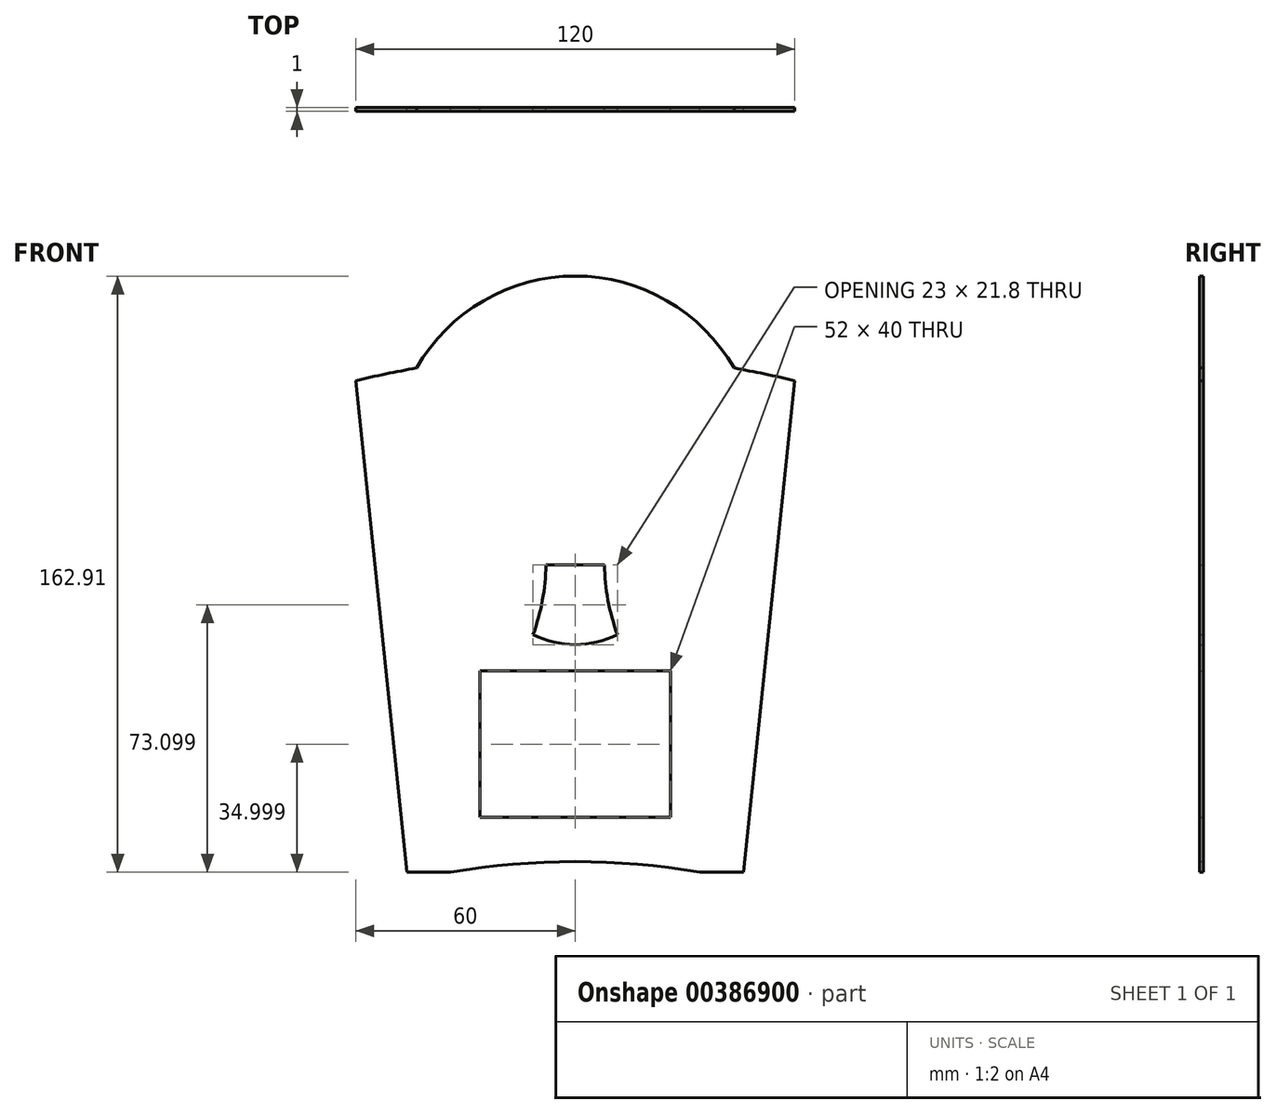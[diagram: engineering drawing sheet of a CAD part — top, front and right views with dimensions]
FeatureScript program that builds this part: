
annotation { "Feature Type Name" : "Feature", "Feature Type Description" : "" }
export const myFeature = defineFeature(function(context is Context, id is Id, definition is map)
    precondition{}
    {
        {
            var Q0;
            Q0=qCreatedBy(makeId("Front.planeOp"),FACE);
            var sketch = newSketch(context, id + "F0", { "sketchPlane" : qUnion([Q0])});
            skLineSegment(sketch, "E0", {"start": v(-46, -93.4) * mm, "end": v(-46, -111.03) * mm, "construction": true});
            skLineSegment(sketch, "E1", {"start": v(-60, 111.9) * mm, "end": v(-60, 93.46) * mm, "construction": true});
            skLineSegment(sketch, "E2", {"start": v(0, 80) * mm, "end": v(15.47, 80) * mm, "construction": true});
            skLineSegment(sketch, "E3", {"start": v(0, -80) * mm, "end": v(14.67, -80) * mm, "construction": true});
            skArc(sketch, "E4", {"start": v(0, 80) * mm, "mid": v(-25.06, 73.27) * mm, "end": v(-43.37, 54.88) * mm});
            skArc(sketch, "E5", {"start": v(0, -80) * mm, "mid": v(-17.06, -80.73) * mm, "end": v(-34, -82.91) * mm});
            skLineSegment(sketch, "E6", {"start": v(-46, -82.91) * mm, "end": v(-60, 51.36) * mm});
            skLineSegment(sketch, "E7", {"start": v(0, 0) * mm, "end": v(0, 20.52) * mm, "construction": true});
            skLineSegment(sketch, "E8", {"start": v(-46, -82.91) * mm, "end": v(-34, -82.91) * mm});
            skArc(sketch, "E9", {"start": v(-60, 51.36) * mm, "mid": v(-51.72, 53.26) * mm, "end": v(-43.37, 54.88) * mm});
            skArc(sketch, "E10.MirrorCS", {"start": v(0, 80) * mm, "mid": v(25.06, 73.27) * mm, "end": v(43.37, 54.88) * mm});
            skArc(sketch, "E11.MirrorCS", {"start": v(60, 51.36) * mm, "mid": v(51.72, 53.26) * mm, "end": v(43.37, 54.88) * mm});
            skLineSegment(sketch, "E12.MirrorCS", {"start": v(46, -82.91) * mm, "end": v(34, -82.91) * mm});
            skLineSegment(sketch, "E13.MirrorCS", {"start": v(46, -82.91) * mm, "end": v(60, 51.36) * mm});
            skArc(sketch, "E14.MirrorCS", {"start": v(0, -80) * mm, "mid": v(17.06, -80.73) * mm, "end": v(34, -82.91) * mm});
            skSolve(sketch);
        }
        {
            var Q0;
            Q0=makeQuery(id+"F0.imprint","IMPRINT",FACE,{"disambiguationData":[TD([[makeQuery(id+"F0.imprint","IMPRINT",EDGE,{"derivedFrom":sQuery(id+"F0.wireOp",EDGE,"E4")}),1.0]])]});
            extrude(context, id + "F1", {"entities" : qUnion([Q0]), "depth" : 1 * mm, "offsetDistance" : 25 * mm});
        }
        {
            var Q0;
            Q0=qCreatedBy(makeId("Front.planeOp"),FACE);
            var sketch = newSketch(context, id + "F2", { "sketchPlane" : qUnion([Q0])});
            skLineSegment(sketch, "E15", {"start": v(-11.5, -17.91) * mm, "end": v(0, -17.91) * mm, "construction": true});
            skLineSegment(sketch, "E16", {"start": v(-8, 1.09) * mm, "end": v(0, 1.09) * mm});
            skArc(sketch, "E17", {"start": v(-11.5, -17.91) * mm, "mid": v(-5.92, -20) * mm, "end": v(0, -20.71) * mm});
            skLineSegment(sketch, "E18", {"start": v(0, 0) * mm, "end": v(0, -3.9) * mm, "construction": true});
            skLineSegment(sketch, "E19.MirrorCS", {"start": v(8, 1.09) * mm, "end": v(0, 1.09) * mm});
            skArc(sketch, "E20.MirrorCS", {"start": v(11.5, -17.91) * mm, "mid": v(5.92, -20) * mm, "end": v(0, -20.71) * mm});
            skLineSegment(sketch, "E21.bottom", {"start": v(26, -27.91) * mm, "end": v(-26, -27.91) * mm});
            skLineSegment(sketch, "E21.top", {"start": v(26, -67.91) * mm, "end": v(-26, -67.91) * mm});
            skLineSegment(sketch, "E21.left", {"start": v(26, -27.91) * mm, "end": v(26, -67.91) * mm});
            skLineSegment(sketch, "E21.right", {"start": v(-26, -27.91) * mm, "end": v(-26, -67.91) * mm});
            skPoint(sketch, "E21.middle", {"position": v(0, -47.91) * mm});
            skArc(sketch, "E22", {"start": v(-11.5, -17.91) * mm, "mid": v(-8.95, -8.56) * mm, "end": v(-8, 1.09) * mm});
            skArc(sketch, "E23.MirrorCS", {"start": v(11.5, -17.91) * mm, "mid": v(8.95, -8.56) * mm, "end": v(8, 1.09) * mm});
            skSolve(sketch);
        }
        {
            var Q0;
            Q0 = qSketchRegion(id + "F2", true);
            extrude(context, id + "F3", {"entities" : qUnion([Q0]), "operationType" : NewBodyOperationType.REMOVE, "endBound" : BoundingType.THROUGH_ALL, "depth" : 25 * mm, "offsetDistance" : 25 * mm});
        }
    });
